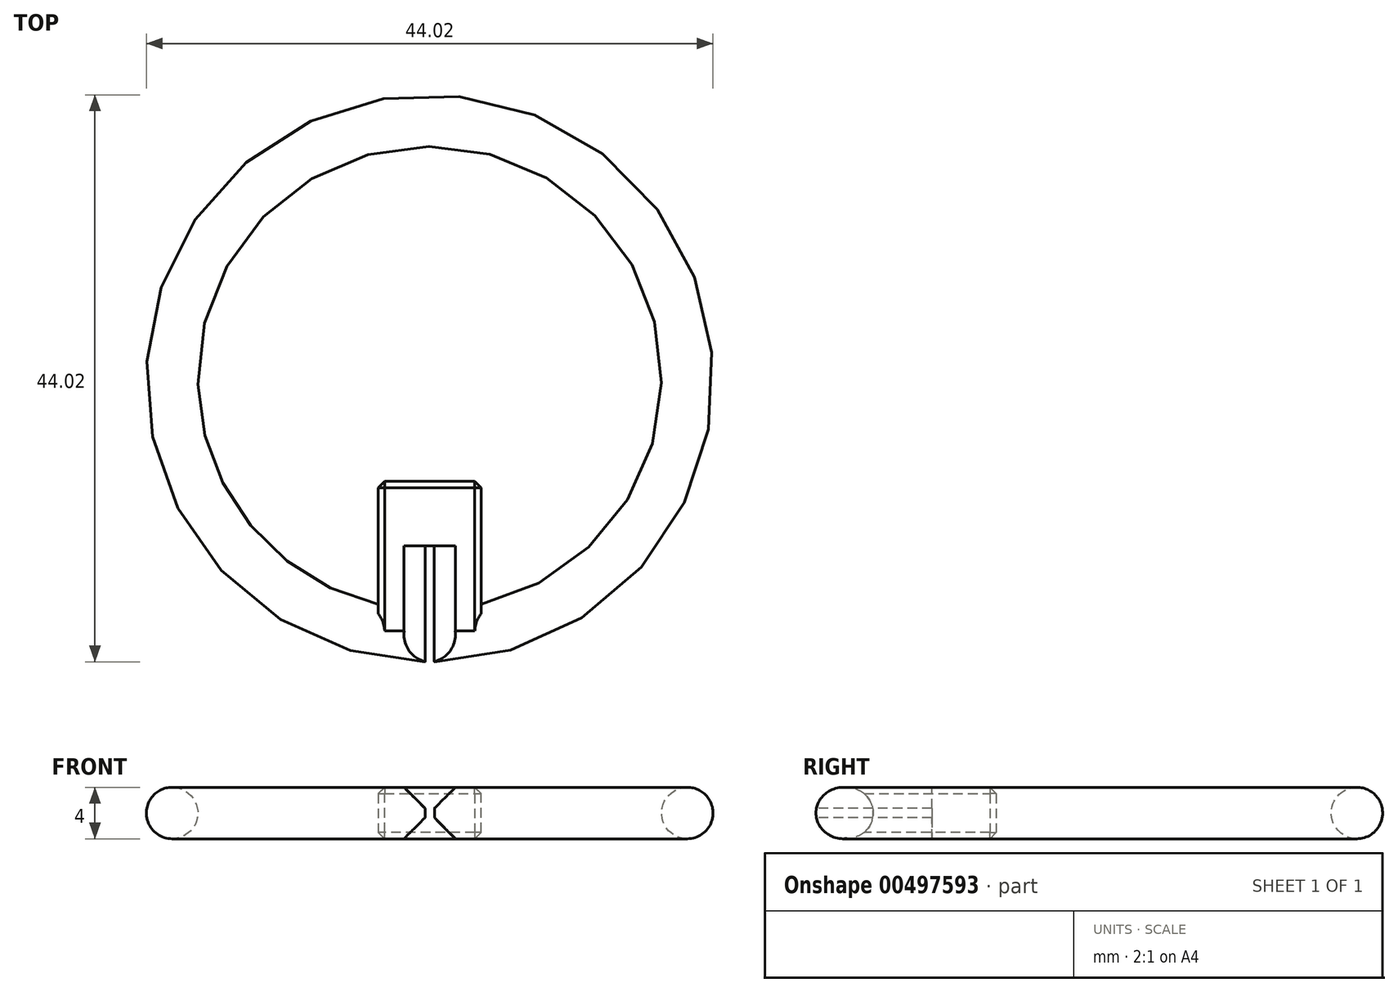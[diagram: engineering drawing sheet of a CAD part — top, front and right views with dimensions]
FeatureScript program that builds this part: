
annotation { "Feature Type Name" : "Feature", "Feature Type Description" : "" }
export const myFeature = defineFeature(function(context is Context, id is Id, definition is map)
    precondition{}
    {
        {
            var Q0;
            Q0=qCreatedBy(makeId("Top.planeOp"),FACE);
            var sketch = newSketch(context, id + "F0", { "sketchPlane" : qUnion([Q0])});
            skLineSegment(sketch, "E0", {"start": v(4, -8) * mm, "end": v(-4, -8) * mm});
            skLineSegment(sketch, "E1", {"start": v(-4, -8) * mm, "end": v(-4, -19.6) * mm});
            skLineSegment(sketch, "E2", {"start": v(-4, -19.6) * mm, "end": v(4, -19.6) * mm});
            skLineSegment(sketch, "E3", {"start": v(4, -19.6) * mm, "end": v(4, -8) * mm});
            skCircle(sketch, "E4", {"center": v(0, 0) * mm, "radius": 20 * mm});
            skSolve(sketch);
        }
        {
            var Q0;
            Q0=qCreatedBy(makeId("Front.planeOp"),FACE);
            var sketch = newSketch(context, id + "F1", { "sketchPlane" : qUnion([Q0])});
            skCircle(sketch, "E5", {"center": v(20.01, 0) * mm, "radius": 2 * mm});
            skSolve(sketch);
        }
        {
            var Q0;
            Q0=makeQuery(id+"F1.imprint","IMPRINT",FACE,{"disambiguationData":[TD([[makeQuery(id+"F1.imprint","IMPRINT",EDGE,{"derivedFrom":sQuery(id+"F1.wireOp",EDGE,"E5")}),1.0]])]});
            var Q1;
            Q1=sQuery(id+"F0.wireOp",EDGE,"E4");
            revolve(context, id + "F2", {"entities" : qUnion([Q0]), "axis" : qUnion([Q1]), "revolveType" : RevolveType.FULL});
        }
        {
            var Q0;
            Q0=makeQuery(id+"F0.imprint","IMPRINT",FACE,{"disambiguationData":[TD([[makeQuery(id+"F0.imprint","IMPRINT",EDGE,{"derivedFrom":sQuery(id+"F0.wireOp",EDGE,"E0")}),1.0]])]});
            extrude(context, id + "F3", {"entities" : qUnion([Q0]), "operationType" : NewBodyOperationType.ADD, "depth" : 2 * mm, "hasSecondDirection" : true, "secondDirectionOppositeDirection" : true, "secondDirectionDepth" : 2 * mm});
        }
        {
            var Q0;
            Q0=makeQuery(id+"F3.opExtrude","SWEPT_FACE",FACE,{"disambiguationData":[OSD([sQuery(id+"F0.wireOp",EDGE,"E0")])]});
            cPlane(context, id + "F4", {"entities" : qUnion([Q0]), "cplaneType" : CPlaneType.OFFSET, "offset" : 15 * mm, "oppositeDirection" : true, "width" : 150 * mm, "height" : 150 * mm});
        }
        {
            var Q0;
            Q0=qCreatedBy(id+"F4.planeOp",FACE);
            var sketch = newSketch(context, id + "F5", { "sketchPlane" : qUnion([Q0])});
            skLineSegment(sketch, "E6", {"start": v(-2, 2) * mm, "end": v(-0.36, 0.36) * mm});
            skLineSegment(sketch, "E7", {"start": v(0.36, 0.36) * mm, "end": v(2, 2) * mm});
            skLineSegment(sketch, "E8", {"start": v(-0.37, -0.37) * mm, "end": v(-2, -2) * mm});
            skLineSegment(sketch, "E9", {"start": v(-2, -2) * mm, "end": v(2, -2) * mm});
            skLineSegment(sketch, "E10", {"start": v(2, -2) * mm, "end": v(0.36, -0.36) * mm});
            skLineSegment(sketch, "E11", {"start": v(2, 2) * mm, "end": v(-2, 2) * mm});
            skLineSegment(sketch, "E12.bottom", {"start": v(-0.36, 0.36) * mm, "end": v(-0.37, 0.36) * mm});
            skLineSegment(sketch, "E12.left", {"start": v(0.36, 0.36) * mm, "end": v(0.36, -0.37) * mm});
            skLineSegment(sketch, "E12.right", {"start": v(-0.37, 0.36) * mm, "end": v(-0.37, -0.37) * mm});
            skSolve(sketch);
        }
        {
            var Q0;
            Q0=makeQuery(id+"F5.imprint","IMPRINT",FACE,{"disambiguationData":[TD([[makeQuery(id+"F5.imprint","IMPRINT",EDGE,{"derivedFrom":sQuery(id+"F5.wireOp",EDGE,"E6")}),1.0]])]});
            extrude(context, id + "F6", {"entities" : qUnion([Q0]), "operationType" : NewBodyOperationType.REMOVE, "depth" : 10 * mm});
        }
        {
            var Q0;
            Q0=makeQuery(id+"F3.opExtrude","CAP_EDGE",EDGE,{"disambiguationData":[OSD([sQuery(id+"F0.wireOp",EDGE,"E1")])],"isStart":false});
            var Q1;
            Q1=makeQuery(id+"F3.opExtrude","CAP_EDGE",EDGE,{"disambiguationData":[OSD([sQuery(id+"F0.wireOp",EDGE,"E0")])],"isStart":false});
            var Q2;
            Q2=makeQuery(id+"F3.opExtrude","CAP_EDGE",EDGE,{"disambiguationData":[OSD([sQuery(id+"F0.wireOp",EDGE,"E3")])],"isStart":false});
            var Q3;
            Q3=makeQuery(id+"F3.opExtrude","CAP_EDGE",EDGE,{"disambiguationData":[OSD([sQuery(id+"F0.wireOp",EDGE,"E3")])],"isStart":true});
            var Q4;
            Q4=makeQuery(id+"F3.opExtrude","CAP_EDGE",EDGE,{"disambiguationData":[OSD([sQuery(id+"F0.wireOp",EDGE,"E0")])],"isStart":true});
            var Q5;
            Q5=makeQuery(id+"F3.opExtrude","CAP_EDGE",EDGE,{"disambiguationData":[OSD([sQuery(id+"F0.wireOp",EDGE,"E1")])],"isStart":true});
            var Q6;
            Q6=makeQuery(id+"F3.opExtrude","SWEPT_EDGE",EDGE,{"disambiguationData":[OSD([sQuery(id+"F0.wireOp",EDGE,"E0"),sQuery(id+"F0.wireOp",EDGE,"E1")])]});
            var Q7;
            Q7=makeQuery(id+"F3.opExtrude","SWEPT_EDGE",EDGE,{"disambiguationData":[OSD([sQuery(id+"F0.wireOp",EDGE,"E0"),sQuery(id+"F0.wireOp",EDGE,"E3")])]});
            chamfer(context, id + "F7", {"entities" : qUnion([Q0, Q1, Q2, Q3, Q4, Q5, Q6, Q7]), "width" : .5 * mm, "tangentPropagation" : true});
        }
    });
